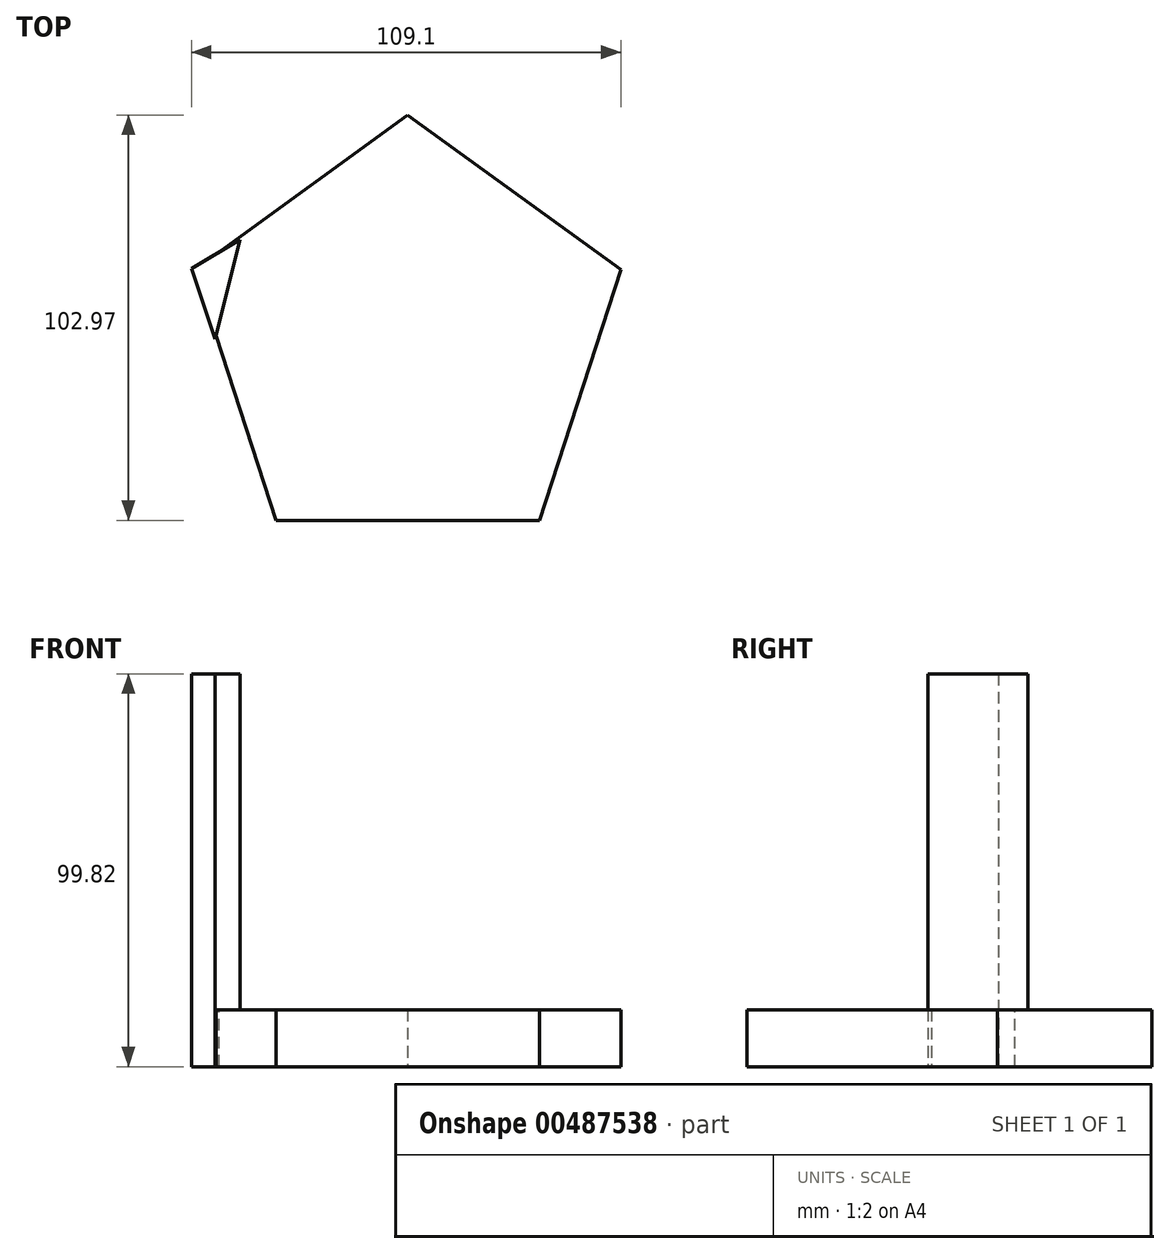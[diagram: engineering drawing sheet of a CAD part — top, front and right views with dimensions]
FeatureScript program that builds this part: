
annotation { "Feature Type Name" : "Feature", "Feature Type Description" : "" }
export const myFeature = defineFeature(function(context is Context, id is Id, definition is map)
    precondition{}
    {
        {
            var Q0;
            Q0=qCreatedBy(makeId("Top.planeOp"),FACE);
            var sketch = newSketch(context, id + "F0", { "sketchPlane" : qUnion([Q0])});
            skCircle(sketch, "E0.cCircle", {"center": v(0, 0) * mm, "radius": 46.05 * mm, "construction": true});
            skLineSegment(sketch, "E0.0", {"start": v(33.46, -46.05) * mm, "end": v(-33.46, -46.05) * mm});
            skLineSegment(sketch, "E0.1", {"start": v(-33.46, -46.05) * mm, "end": v(-54.13, 17.59) * mm});
            skLineSegment(sketch, "E0.2", {"start": v(-54.13, 17.59) * mm, "end": v(0, 56.92) * mm});
            skLineSegment(sketch, "E0.3", {"start": v(0, 56.92) * mm, "end": v(54.13, 17.59) * mm});
            skLineSegment(sketch, "E0.4", {"start": v(54.13, 17.59) * mm, "end": v(33.46, -46.05) * mm});
            skPoint(sketch, "E0.0.midPoint", {"position": v(0, -46.05) * mm});
            skSolve(sketch);
        }
        {
            var Q0;
            Q0=makeQuery(id+"F0.imprint","IMPRINT",FACE,{"disambiguationData":[TD([[makeQuery(id+"F0.imprint","IMPRINT",EDGE,{"derivedFrom":sQuery(id+"F0.wireOp",EDGE,"E0.0")}),-1.0]])]});
            extrude(context, id + "F1", {"entities" : qUnion([Q0]), "depth" : 14.48 * mm});
        }
        {
            var Q0;
            Q0=qCreatedBy(makeId("Top.planeOp"),FACE);
            var sketch = newSketch(context, id + "F2", { "sketchPlane" : qUnion([Q0])});
            skLineSegment(sketch, "E1", {"start": v(-54.97, 17.84) * mm, "end": v(-48.93, 0) * mm});
            skLineSegment(sketch, "E2", {"start": v(-48.93, 0) * mm, "end": v(-42.6, 25.33) * mm});
            skLineSegment(sketch, "E3", {"start": v(-42.6, 25.33) * mm, "end": v(-54.97, 17.84) * mm});
            skSolve(sketch);
        }
        {
            var Q0;
            Q0=makeQuery(id+"F2.imprint","IMPRINT",FACE,{"disambiguationData":[TD([[makeQuery(id+"F2.imprint","IMPRINT",EDGE,{"derivedFrom":sQuery(id+"F2.wireOp",EDGE,"E1")}),1.0]])]});
            extrude(context, id + "F3", {"entities" : qUnion([Q0]), "operationType" : NewBodyOperationType.ADD, "depth" : 99.82 * mm});
        }
    });
